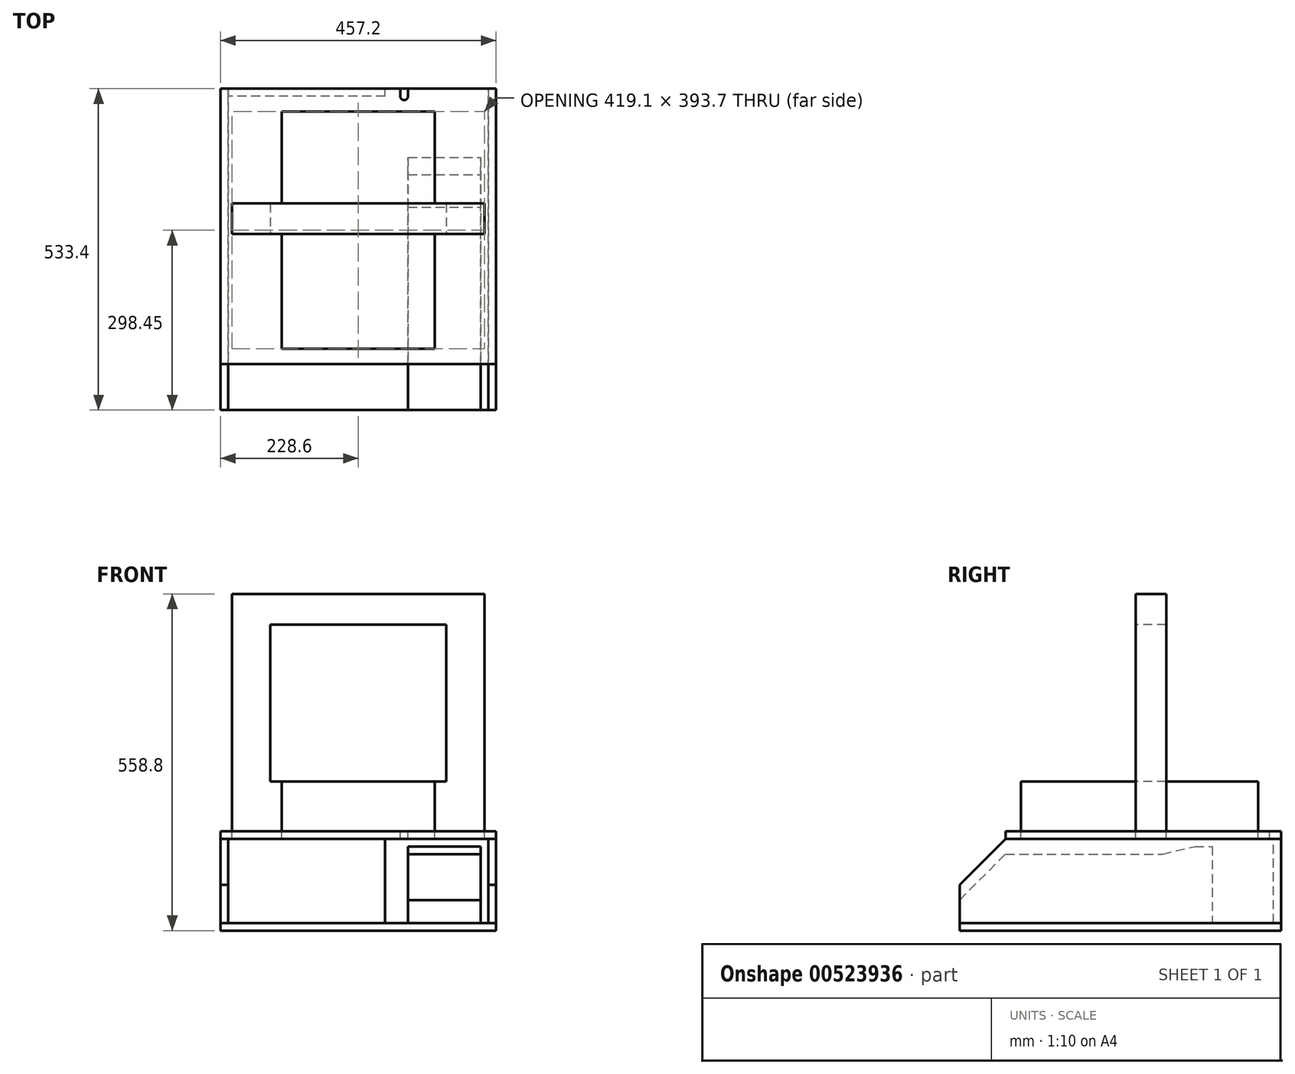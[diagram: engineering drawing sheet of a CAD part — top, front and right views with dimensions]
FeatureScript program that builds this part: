
annotation { "Feature Type Name" : "Feature", "Feature Type Description" : "" }
export const myFeature = defineFeature(function(context is Context, id is Id, definition is map)
    precondition{}
    {
        {
            var Q0;
            Q0=qCreatedBy(makeId("Front.planeOp"),FACE);
            var sketch = newSketch(context, id + "F0", { "sketchPlane" : qUnion([Q0])});
            skLineSegment(sketch, "E0.bottom", {"start": v(0, 0) * mm, "end": v(419.1, 0) * mm});
            skLineSegment(sketch, "E0.top", {"start": v(0, 393.7) * mm, "end": v(419.1, 393.7) * mm});
            skLineSegment(sketch, "E0.left", {"start": v(0, 0) * mm, "end": v(0, 393.7) * mm});
            skLineSegment(sketch, "E0.right", {"start": v(419.1, 0) * mm, "end": v(419.1, 393.7) * mm});
            skLineSegment(sketch, "E1.bottom", {"start": v(63.5, 342.9) * mm, "end": v(355.6, 342.9) * mm});
            skLineSegment(sketch, "E1.top", {"start": v(63.5, 82.55) * mm, "end": v(355.6, 82.55) * mm});
            skLineSegment(sketch, "E1.left", {"start": v(63.5, 342.9) * mm, "end": v(63.5, 82.55) * mm});
            skLineSegment(sketch, "E1.right", {"start": v(355.6, 342.9) * mm, "end": v(355.6, 82.55) * mm});
            skSolve(sketch);
        }
        {
            var Q0;
            Q0=makeQuery(id+"F0.imprint","IMPRINT",FACE,{"disambiguationData":[TD([[makeQuery(id+"F0.imprint","IMPRINT",EDGE,{"derivedFrom":sQuery(id+"F0.wireOp",EDGE,"E0.bottom")}),1.0]])]});
            extrude(context, id + "F1", {"entities" : qUnion([Q0]), "oppositeDirection" : true, "depth" : 50.8 * mm, "offsetDistance" : 25.4 * mm});
        }
        {
            var Q0;
            Q0=makeQuery(id+"F1.opExtrude","CAP_FACE",FACE,{"disambiguationData":[OSD([sQuery(id+"F0.wireOp",EDGE,"E0.bottom"),sQuery(id+"F0.wireOp",EDGE,"E0.top"),sQuery(id+"F0.wireOp",EDGE,"E0.left"),sQuery(id+"F0.wireOp",EDGE,"E0.right"),sQuery(id+"F0.wireOp",EDGE,"E1.bottom"),sQuery(id+"F0.wireOp",EDGE,"E1.top"),sQuery(id+"F0.wireOp",EDGE,"E1.left"),sQuery(id+"F0.wireOp",EDGE,"E1.right")])],"isStart":true});
            var sketch = newSketch(context, id + "F2", { "sketchPlane" : qUnion([Q0])});
            skLineSegment(sketch, "E2.bottom", {"start": v(82.55, 0) * mm, "end": v(336.55, 0) * mm});
            skLineSegment(sketch, "E2.top", {"start": v(82.55, 82.55) * mm, "end": v(336.55, 82.55) * mm});
            skLineSegment(sketch, "E2.left", {"start": v(82.55, 0) * mm, "end": v(82.55, 82.55) * mm});
            skLineSegment(sketch, "E2.right", {"start": v(336.55, 0) * mm, "end": v(336.55, 82.55) * mm});
            skSolve(sketch);
        }
        {
            var Q0;
            Q0=makeQuery(id+"F2.imprint","IMPRINT",FACE,{"disambiguationData":[TD([[makeQuery(id+"F2.imprint","IMPRINT",EDGE,{"derivedFrom":sQuery(id+"F2.wireOp",EDGE,"E2.bottom")}),1.0]])]});
            extrude(context, id + "F3", {"entities" : qUnion([Q0]), "operationType" : NewBodyOperationType.ADD, "depth" : 190.5 * mm, "offsetDistance" : 25.4 * mm});
        }
        {
            var Q0;
            Q0=makeQuery(id+"F3.opExtrude","CAP_FACE",FACE,{"disambiguationData":[OSD([sQuery(id+"F2.wireOp",EDGE,"E2.bottom"),sQuery(id+"F2.wireOp",EDGE,"E2.top"),sQuery(id+"F2.wireOp",EDGE,"E2.left"),sQuery(id+"F2.wireOp",EDGE,"E2.right")])],"isStart":false});
            extrude(context, id + "F4", {"entities" : qUnion([Q0]), "operationType" : NewBodyOperationType.ADD, "oppositeDirection" : true, "depth" : 393.7 * mm, "offsetDistance" : 25.4 * mm});
        }
        {
            var Q0;
            {var subQ0=sQuery(id+"F2.wireOp",EDGE,"E2.bottom");Q0=makeQuery(id+"F4.boolean.opBoolean","MERGE",FACE,{"derivedFrom":[makeQuery(id+"F3.boolean.opBoolean","MERGE",FACE,{"derivedFrom":[makeQuery(id+"F1.opExtrude","SWEPT_FACE",FACE,{"disambiguationData":[OSD([sQuery(id+"F0.wireOp",EDGE,"E0.bottom")])]}),makeQuery(id+"F3.opExtrude","SWEPT_FACE",FACE,{"disambiguationData":[OSD([subQ0])]})]}),makeQuery(id+"F4.opExtrude","SWEPT_FACE",FACE,{"disambiguationData":[OSD([subQ0])]})]});}
            var sketch = newSketch(context, id + "F5", { "sketchPlane" : qUnion([Q0])});
            skLineSegment(sketch, "E3.bottom", {"start": v(-19.05, -241.3) * mm, "end": v(438.15, -241.3) * mm});
            skLineSegment(sketch, "E3.top", {"start": v(-19.05, 215.9) * mm, "end": v(438.15, 215.9) * mm});
            skLineSegment(sketch, "E3.left", {"start": v(-19.05, -241.3) * mm, "end": v(-19.05, 215.9) * mm});
            skLineSegment(sketch, "E3.right", {"start": v(438.15, -241.3) * mm, "end": v(438.15, 215.9) * mm});
            skLineSegment(sketch, "E4", {"start": v(209.55, 190.5) * mm, "end": v(209.55, 215.9) * mm, "construction": true});
            skLineSegment(sketch, "E5", {"start": v(209.55, -241.3) * mm, "end": v(209.55, -203.2) * mm, "construction": true});
            skSolve(sketch);
        }
        {
            var Q0;
            Q0=makeQuery(id+"F5.imprint","IMPRINT",FACE,{"disambiguationData":[TD([[makeQuery(id+"F5.imprint","IMPRINT",EDGE,{"derivedFrom":sQuery(id+"F5.wireOp",EDGE,"E3.bottom")}),1.0]])]});
            var Q1;
            {var subQ1=sQuery(id+"F2.wireOp",EDGE,"E2.bottom");Q1=makeQuery(id+"F5.imprint","IMPRINT",FACE,{"disambiguationData":[TD([[makeQuery(id+"F5.imprint","IMPRINT",EDGE,{"derivedFrom":makeQuery(id+"F3.opExtrude","CAP_EDGE",EDGE,{"disambiguationData":[OSD([subQ1])],"isStart":false})}),-1.0]])]});}
            extrude(context, id + "F6", {"entities" : qUnion([Q0, Q1]), "depth" : 12.7 * mm, "offsetDistance" : 25.4 * mm});
        }
        {
            var Q0;
            Q0=makeQuery(id+"F6.opExtrude","CAP_FACE",FACE,{"disambiguationData":[OSD([sQuery(id+"F5.wireOp",EDGE,"E3.bottom"),sQuery(id+"F5.wireOp",EDGE,"E3.top"),sQuery(id+"F5.wireOp",EDGE,"E3.left"),sQuery(id+"F5.wireOp",EDGE,"E3.right")])],"isStart":false});
            cPlane(context, id + "F7", {"entities" : qUnion([Q0]), "cplaneType" : CPlaneType.OFFSET, "offset" : 139.7 * mm, "width" : 152.4 * mm, "height" : 152.4 * mm});
        }
        {
            var Q0;
            Q0=qCreatedBy(id+"F7.planeOp",FACE);
            var sketch = newSketch(context, id + "F8", { "sketchPlane" : qUnion([Q0])});
            skLineSegment(sketch, "E6.0.0", {"start": v(438.15, 215.9) * mm, "end": v(-19.05, 215.9) * mm});
            skLineSegment(sketch, "E6.0.1", {"start": v(-19.05, 215.9) * mm, "end": v(-19.05, -241.3) * mm});
            skLineSegment(sketch, "E6.0.2", {"start": v(-19.05, -241.3) * mm, "end": v(438.15, -241.3) * mm});
            skLineSegment(sketch, "E6.0.3", {"start": v(438.15, -241.3) * mm, "end": v(438.15, 215.9) * mm});
            skLineSegment(sketch, "E7", {"start": v(-19.05, 215.9) * mm, "end": v(-19.05, 292.1) * mm});
            skLineSegment(sketch, "E8", {"start": v(-19.05, 292.1) * mm, "end": v(438.15, 292.1) * mm});
            skLineSegment(sketch, "E9", {"start": v(438.15, 292.1) * mm, "end": v(438.15, 215.9) * mm});
            skSolve(sketch);
        }
        {
            var Q0;
            Q0=makeQuery(id+"F8.imprint","IMPRINT",FACE,{"disambiguationData":[TD([[makeQuery(id+"F8.imprint","IMPRINT",EDGE,{"derivedFrom":sQuery(id+"F8.wireOp",EDGE,"E6.0.0")}),-1.0]])]});
            var Q1;
            Q1=makeQuery(id+"F8.imprint","IMPRINT",FACE,{"disambiguationData":[TD([[makeQuery(id+"F8.imprint","IMPRINT",EDGE,{"derivedFrom":sQuery(id+"F8.wireOp",EDGE,"E6.0.0")}),1.0]])]});
            extrude(context, id + "F9", {"entities" : qUnion([Q0, Q1]), "depth" : 12.7 * mm, "offsetDistance" : 25.4 * mm});
        }
        {
            var Q0;
            Q0=makeQuery(id+"F9.opExtrude","SWEPT_FACE",FACE,{"disambiguationData":[OSD([sQuery(id+"F8.wireOp",EDGE,"E6.0.3"),sQuery(id+"F8.wireOp",EDGE,"E9")])]});
            cPlane(context, id + "F10", {"entities" : qUnion([Q0]), "cplaneType" : CPlaneType.OFFSET, "offset" : 25.4 * mm, "oppositeDirection" : true, "width" : 152.4 * mm, "height" : 152.4 * mm});
        }
        {
            var Q0;
            Q0=qCreatedBy(id+"F10.planeOp",FACE);
            var sketch = newSketch(context, id + "F11", { "sketchPlane" : qUnion([Q0])});
            skLineSegment(sketch, "E10.0.0", {"start": v(241.3, -152.4) * mm, "end": v(-292.1, -152.4) * mm});
            skLineSegment(sketch, "E10.0.2", {"start": v(-292.1, -152.4) * mm, "end": v(241.3, -152.4) * mm});
            skLineSegment(sketch, "E11", {"start": v(-292.1, -152.4) * mm, "end": v(-292.1, -114.3) * mm});
            skLineSegment(sketch, "E12", {"start": v(-292.1, -114.3) * mm, "end": v(-215.9, -38.1) * mm});
            skLineSegment(sketch, "E13", {"start": v(-215.9, -38.1) * mm, "end": v(44.45, -38.1) * mm});
            skLineSegment(sketch, "E14", {"start": v(44.45, -38.1) * mm, "end": v(98.43, -25.4) * mm});
            skLineSegment(sketch, "E15", {"start": v(98.43, -25.4) * mm, "end": v(127, -25.4) * mm});
            skLineSegment(sketch, "E16", {"start": v(127, -25.4) * mm, "end": v(127, -152.4) * mm});
            skSolve(sketch);
        }
        {
            var Q0;
            {var subQ0=sQuery(id+"F11.wireOp",EDGE,"E11");Q0=makeQuery(id+"F11.imprint","IMPRINT",FACE,{"disambiguationData":[TD([[makeQuery(id+"F11.imprint","IMPRINT",EDGE,{"derivedFrom":subQ0}),-1.0]])]});}
            extrude(context, id + "F12", {"entities" : qUnion([Q0]), "oppositeDirection" : true, "depth" : 120.65 * mm, "offsetDistance" : 25.4 * mm});
        }
        {
            var Q0;
            Q0=makeQuery(id+"F6.opExtrude","SWEPT_FACE",FACE,{"disambiguationData":[OSD([sQuery(id+"F5.wireOp",EDGE,"E3.right")])]});
            var sketch = newSketch(context, id + "F13", { "sketchPlane" : qUnion([Q0])});
            skLineSegment(sketch, "E17.0", {"start": v(241.3, -12.7) * mm, "end": v(-215.9, -12.7) * mm});
            skLineSegment(sketch, "E18.0", {"start": v(-292.1, -152.4) * mm, "end": v(241.3, -152.4) * mm});
            skLineSegment(sketch, "E19", {"start": v(241.3, -152.4) * mm, "end": v(241.3, -12.7) * mm});
            skLineSegment(sketch, "E20", {"start": v(-215.9, -12.7) * mm, "end": v(-292.1, -88.9) * mm});
            skLineSegment(sketch, "E21", {"start": v(-292.1, -88.9) * mm, "end": v(-292.1, -152.4) * mm});
            skSolve(sketch);
        }
        {
            var Q0;
            Q0=makeQuery(id+"F13.imprint","IMPRINT",FACE,{"disambiguationData":[TD([[makeQuery(id+"F13.imprint","IMPRINT",EDGE,{"derivedFrom":sQuery(id+"F13.wireOp",EDGE,"E17.0")}),1.0]])]});
            extrude(context, id + "F14", {"entities" : qUnion([Q0]), "oppositeDirection" : true, "depth" : 12.7 * mm, "offsetDistance" : 25.4 * mm});
        }
        {
            var Q0;
            Q0=makeQuery(id+"F6.opExtrude","SWEPT_FACE",FACE,{"disambiguationData":[OSD([sQuery(id+"F5.wireOp",EDGE,"E3.right")])]});
            var Q1;
            Q1=makeQuery(id+"F6.opExtrude","SWEPT_FACE",FACE,{"disambiguationData":[OSD([sQuery(id+"F5.wireOp",EDGE,"E3.left")])]});
            cPlane(context, id + "F15", {"entities" : qUnion([Q0, Q1]), "cplaneType" : CPlaneType.MID_PLANE, "offset" : 25.4 * mm, "width" : 152.4 * mm, "height" : 152.4 * mm});
        }
        {
            var Q0;
            Q0=makeQuery(id+"F14.opExtrude","SWEPT_BODY",BODY,{"disambiguationData":[OSD([sQuery(id+"F13.wireOp",EDGE,"E17.0"),sQuery(id+"F13.wireOp",EDGE,"E18.0"),sQuery(id+"F13.wireOp",EDGE,"E19"),sQuery(id+"F13.wireOp",EDGE,"E20"),sQuery(id+"F13.wireOp",EDGE,"E21")])]});
            var Q1;
            Q1=qCreatedBy(id+"F15.planeOp",FACE);
            mirror(context, id + "F16", {"entities" : qUnion([Q0]), "mirrorPlane" : qUnion([Q1])});
        }
        {
            var Q0;
            Q0=makeQuery(id+"F16.opPattern","COPY",FACE,{"derivedFrom":makeQuery(id+"F14.opExtrude","SWEPT_FACE",FACE,{"disambiguationData":[OSD([sQuery(id+"F13.wireOp",EDGE,"E19")])]}),"instanceName":"1"});
            var sketch = newSketch(context, id + "F17", { "sketchPlane" : qUnion([Q0])});
            skLineSegment(sketch, "E22.0", {"start": v(-292.1, -25.4) * mm, "end": v(-292.1, -152.4) * mm});
            skLineSegment(sketch, "E23", {"start": v(-254, -12.7) * mm, "end": v(6.35, -12.7) * mm});
            skLineSegment(sketch, "E24", {"start": v(6.35, -12.7) * mm, "end": v(6.35, -152.4) * mm});
            skLineSegment(sketch, "E25", {"start": v(6.35, -152.4) * mm, "end": v(-254, -152.4) * mm});
            skLineSegment(sketch, "E26", {"start": v(-254, -152.4) * mm, "end": v(-254, -12.7) * mm});
            skSolve(sketch);
        }
        {
            var Q0;
            Q0=makeQuery(id+"F17.imprint","IMPRINT",FACE,{"disambiguationData":[TD([[makeQuery(id+"F17.imprint","IMPRINT",EDGE,{"derivedFrom":sQuery(id+"F17.wireOp",EDGE,"E23")}),-1.0]])]});
            extrude(context, id + "F18", {"entities" : qUnion([Q0]), "oppositeDirection" : true, "depth" : 12.7 * mm, "offsetDistance" : 25.4 * mm});
        }
        {
            var Q0;
            Q0=makeQuery(id+"F6.opExtrude","CAP_FACE",FACE,{"disambiguationData":[OSD([sQuery(id+"F5.wireOp",EDGE,"E3.bottom"),sQuery(id+"F5.wireOp",EDGE,"E3.top"),sQuery(id+"F5.wireOp",EDGE,"E3.left"),sQuery(id+"F5.wireOp",EDGE,"E3.right")])],"isStart":true});
            var sketch = newSketch(context, id + "F19", { "sketchPlane" : qUnion([Q0])});
            skPoint(sketch, "E27.0", {"position": v(292.1, 127) * mm});
            skLineSegment(sketch, "E28", {"start": v(292.1, 127) * mm, "end": v(292.1, 241.3) * mm});
            skCircle(sketch, "E29", {"center": v(285.75, 228.6) * mm, "radius": 6.35 * mm});
            skLineSegment(sketch, "E30", {"start": v(279.4, 228.6) * mm, "end": v(279.4, 241.3) * mm});
            skSolve(sketch);
        }
        {
            var Q0;
            {var subQ0=sQuery(id+"F19.wireOp",EDGE,"E29");var subQ1=makeQuery(id+"F19.imprint","INTERSECT",VERTEX,{"derivedFrom":[subQ0,sQuery(id+"F19.wireOp",EDGE,"E30")]});Q0=makeQuery(id+"F19.imprint","IMPRINT",FACE,{"disambiguationData":[TD([[makeQuery(id+"F19.imprint","IMPRINT",EDGE,{"disambiguationData":[TD([[subQ1,1.0]])],"derivedFrom":subQ0}),1.0]])]});}
            var Q1;
            {var subQ5=sQuery(id+"F19.wireOp",EDGE,"E30");Q1=makeQuery(id+"F19.imprint","IMPRINT",FACE,{"disambiguationData":[TD([[makeQuery(id+"F19.imprint","IMPRINT",EDGE,{"derivedFrom":subQ5}),-1.0]])]});}
            extrude(context, id + "F20", {"entities" : qUnion([Q0, Q1]), "operationType" : NewBodyOperationType.REMOVE, "endBound" : BoundingType.UP_TO_NEXT, "oppositeDirection" : true, "depth" : 25.4 * mm, "offsetDistance" : 25.4 * mm});
        }
    });
